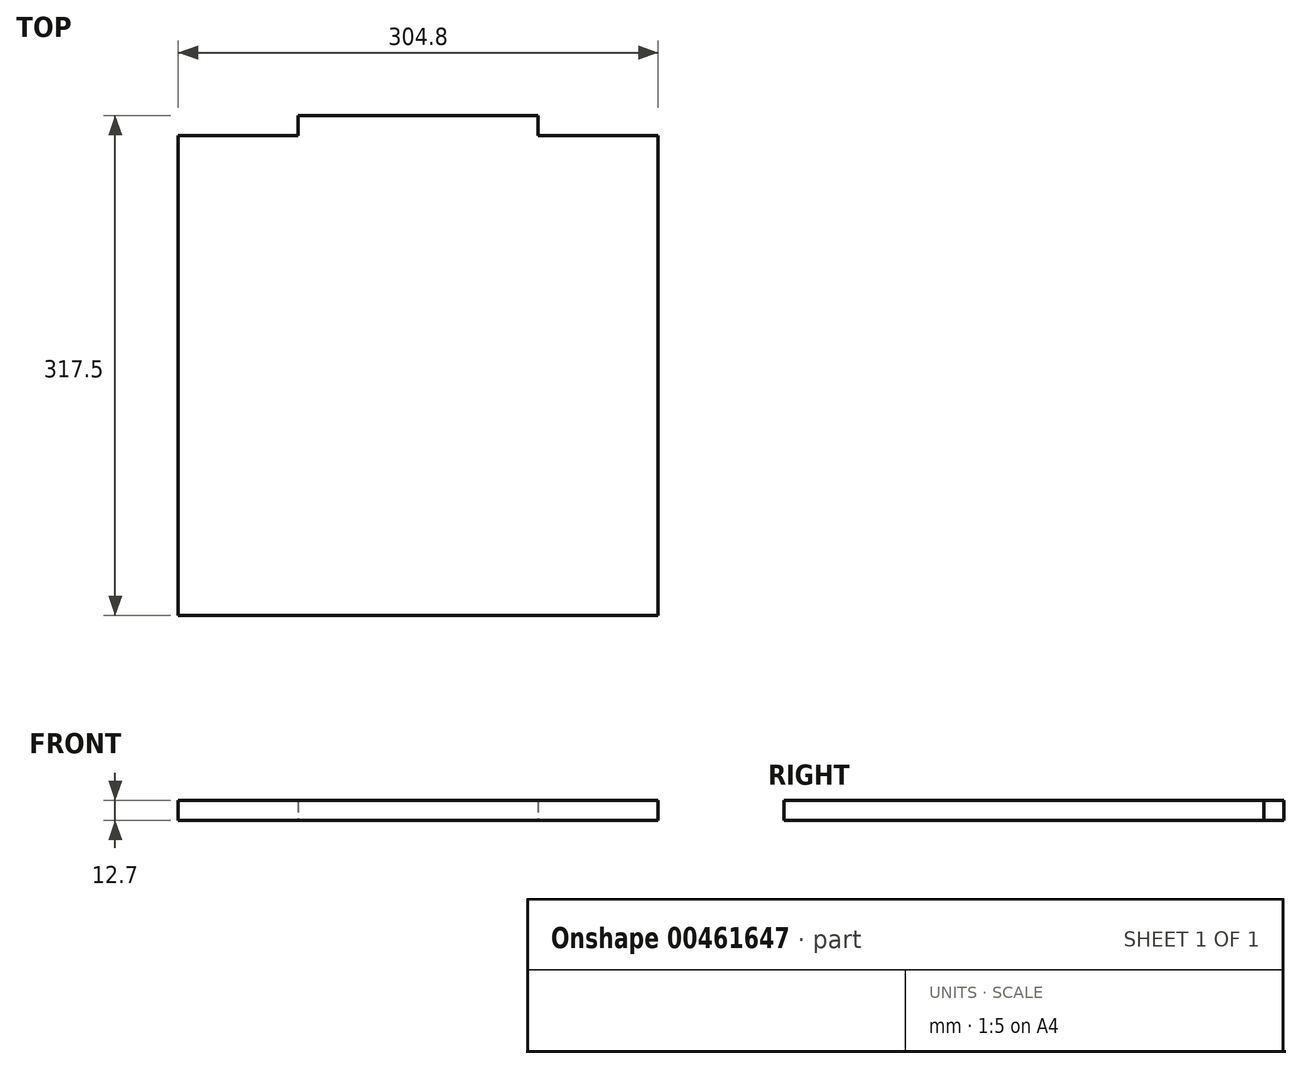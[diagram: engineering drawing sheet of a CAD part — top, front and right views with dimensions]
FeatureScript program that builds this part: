
annotation { "Feature Type Name" : "Feature", "Feature Type Description" : "" }
export const myFeature = defineFeature(function(context is Context, id is Id, definition is map)
    precondition{}
    {
        {
            var Q0;
            Q0=qCreatedBy(makeId("Top.planeOp"),FACE);
            var sketch = newSketch(context, id + "F0", { "sketchPlane" : qUnion([Q0])});
            skLineSegment(sketch, "E0.bottom", {"start": v(152.4, 152.4) * mm, "end": v(-152.4, 152.4) * mm});
            skLineSegment(sketch, "E0.top", {"start": v(152.4, -152.4) * mm, "end": v(-152.4, -152.4) * mm});
            skLineSegment(sketch, "E0.left", {"start": v(152.4, 152.4) * mm, "end": v(152.4, -152.4) * mm});
            skLineSegment(sketch, "E0.right", {"start": v(-152.4, 152.4) * mm, "end": v(-152.4, -152.4) * mm});
            skPoint(sketch, "E0.middle", {"position": v(0, 0) * mm});
            skLineSegment(sketch, "E1.bottom", {"start": v(-76.2, 152.4) * mm, "end": v(76.2, 152.4) * mm});
            skLineSegment(sketch, "E1.top", {"start": v(-76.2, 165.1) * mm, "end": v(76.2, 165.1) * mm});
            skLineSegment(sketch, "E1.left", {"start": v(-76.2, 152.4) * mm, "end": v(-76.2, 165.1) * mm});
            skLineSegment(sketch, "E1.right", {"start": v(76.2, 152.4) * mm, "end": v(76.2, 165.1) * mm});
            skSolve(sketch);
        }
        {
            var Q0;
            Q0 = qSketchRegion(id + "F0", true);
            extrude(context, id + "F1", {"entities" : qUnion([Q0]), "depth" : 12.7 * mm});
        }
    });
